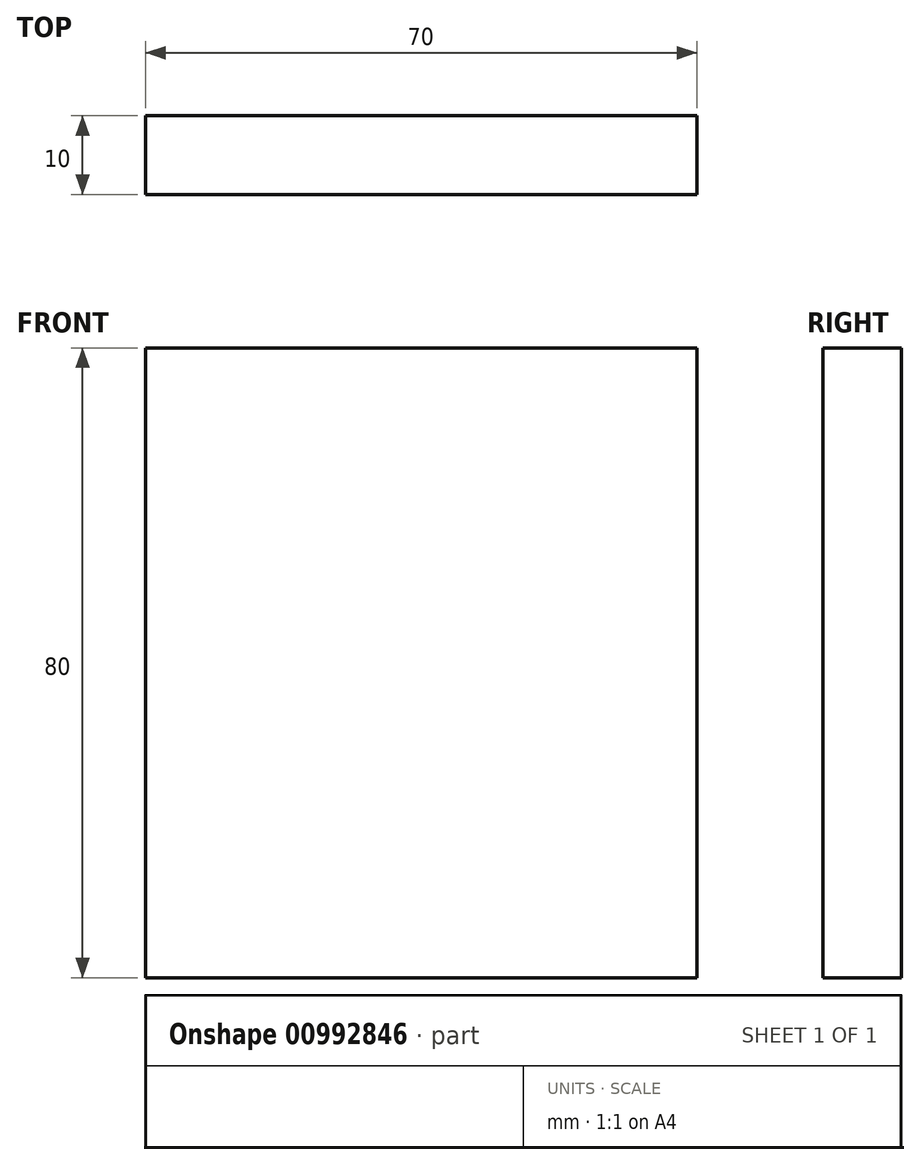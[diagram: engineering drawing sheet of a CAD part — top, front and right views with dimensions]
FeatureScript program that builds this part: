
annotation { "Feature Type Name" : "Feature", "Feature Type Description" : "" }
export const myFeature = defineFeature(function(context is Context, id is Id, definition is map)
    precondition{}
    {
        {
            var Q0;
            Q0=qCreatedBy(makeId("Front.planeOp"),FACE);
            var sketch = newSketch(context, id + "F0", { "sketchPlane" : qUnion([Q0])});
            skLineSegment(sketch, "E0.bottom", {"start": v(35, -40) * mm, "end": v(-35, -40) * mm});
            skLineSegment(sketch, "E0.top", {"start": v(35, 40) * mm, "end": v(-35, 40) * mm});
            skLineSegment(sketch, "E0.left", {"start": v(35, -40) * mm, "end": v(35, 40) * mm});
            skLineSegment(sketch, "E0.right", {"start": v(-35, -40) * mm, "end": v(-35, 40) * mm});
            skPoint(sketch, "E0.middle", {"position": v(0, 0) * mm});
            skSolve(sketch);
        }
        {
            var Q0;
            Q0=makeQuery(id+"F0.imprint","IMPRINT",FACE,{"disambiguationData":[TD([[makeQuery(id+"F0.imprint","IMPRINT",EDGE,{"derivedFrom":sQuery(id+"F0.wireOp",EDGE,"E0.bottom")}),-1.0]])]});
            extrude(context, id + "F1", {"entities" : qUnion([Q0]), "depth" : 10 * mm, "offsetDistance" : 25 * mm});
        }
    });
